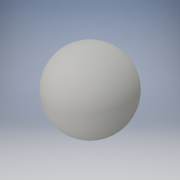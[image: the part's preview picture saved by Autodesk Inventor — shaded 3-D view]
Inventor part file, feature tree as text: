
AUTODESK INVENTOR PART (.ipt)
format: ipt  version: 2016 (Build 200138000, 138)  size: 118,272 bytes
history: native  units: in
note: dims shown in document units (in); Inventor stores cm internally (conversion verified against a paired STEP export)
features: plane x6, revolve x1, sketch x1
ambient origin geometry x8: Origin, YZ Plane, XZ Plane, XY Plane, X Axis, Y Axis, Z Axis, Center Point
bodies: Solid1 (feature_tree)
feature tree (8):
  revolve  "Revolution1"  [1 undecoded]
  plane  "Work Plane1"
  plane  "Work Plane2"
  plane  "Work Plane4"
  plane  "Work Plane5"
  plane  "Work Plane6"
  plane  "Work Plane7"
  sketch  "Sketch1"  dims[d0=10.0in d1=5.0in d2=90.0deg d3=-10.0in d5=10.0in d6=5.0in d7=-5.0in d8=-5.0in]
note: 1 required parameter value undecoded (feature->parameter linkage not recoverable at this tier; creation-order binding heuristic only, values carry confidence <= 0.55)
